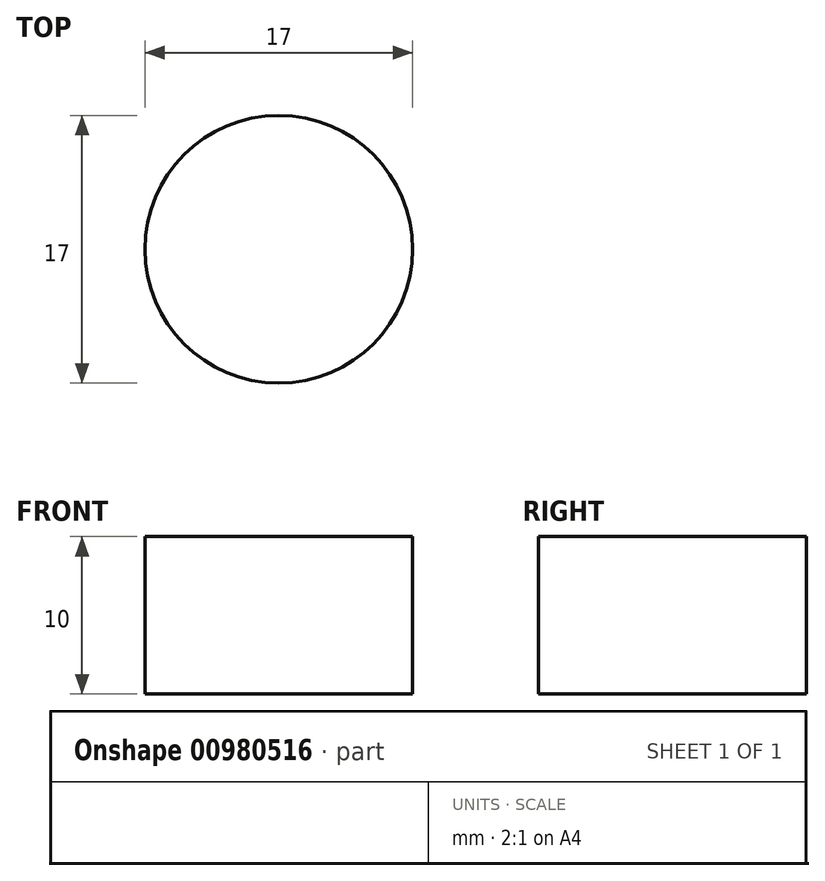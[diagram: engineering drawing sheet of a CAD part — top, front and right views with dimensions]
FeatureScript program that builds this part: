
annotation { "Feature Type Name" : "Feature", "Feature Type Description" : "" }
export const myFeature = defineFeature(function(context is Context, id is Id, definition is map)
    precondition{}
    {
        {
            var Q0;
            Q0=qCreatedBy(makeId("Top.planeOp"),FACE);
            var sketch = newSketch(context, id + "F0", { "sketchPlane" : qUnion([Q0])});
            skCircle(sketch, "E0", {"center": v(0, 0) * mm, "radius": 8.5 * mm});
            skSolve(sketch);
        }
        {
            var Q0;
            Q0=makeQuery(id+"F0.imprint","IMPRINT",FACE,{"disambiguationData":[TD([[makeQuery(id+"F0.imprint","IMPRINT",EDGE,{"derivedFrom":sQuery(id+"F0.wireOp",EDGE,"E0")}),1.0]])]});
            extrude(context, id + "F1", {"entities" : qUnion([Q0]), "depth" : 10 * mm, "offsetDistance" : 25.4 * mm});
        }
    });
